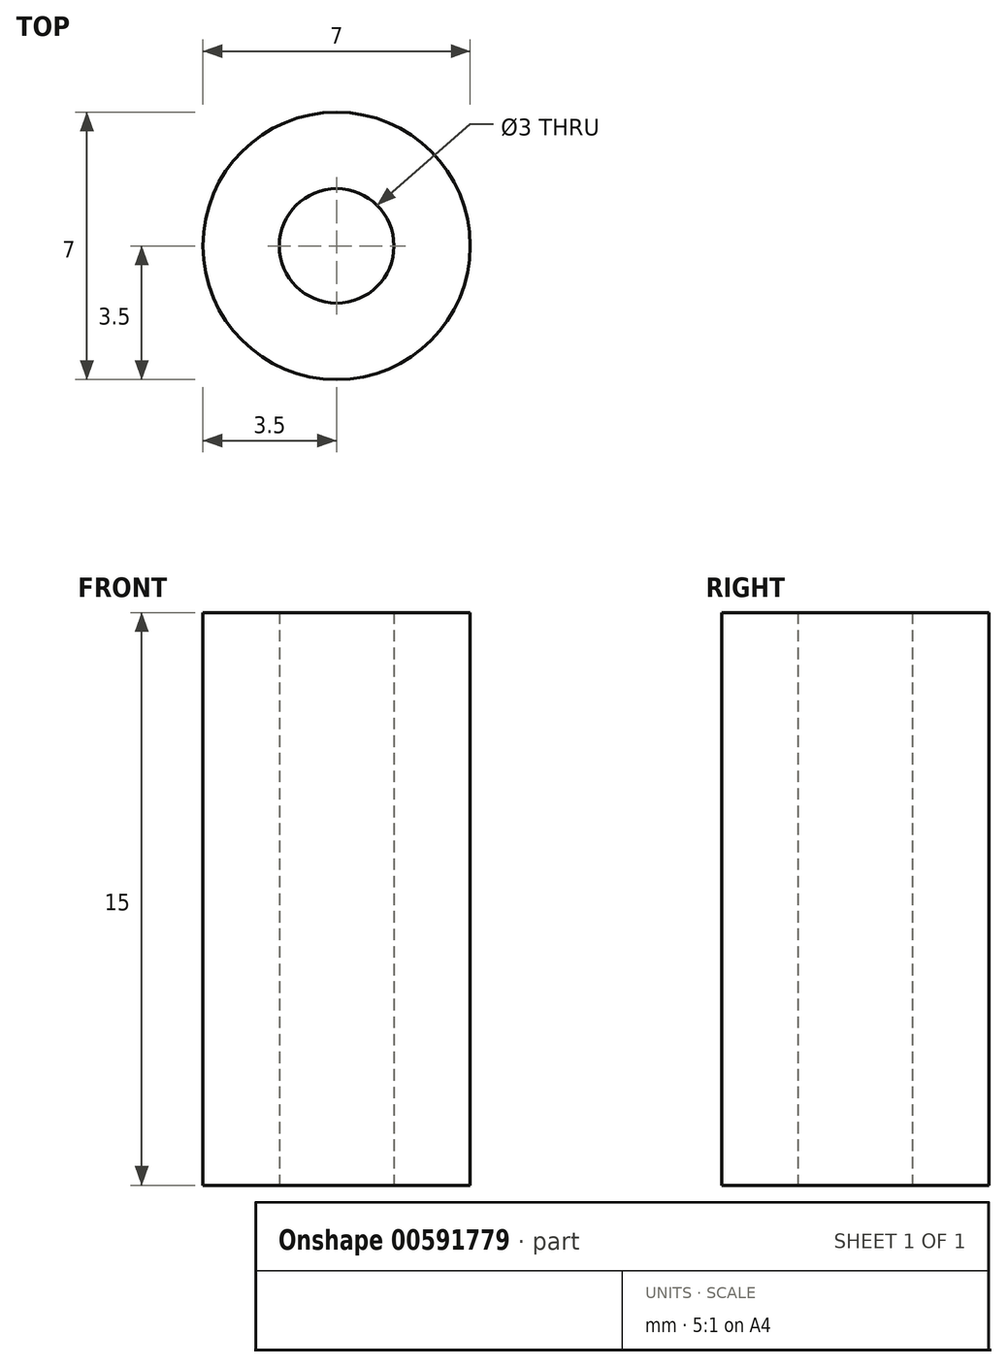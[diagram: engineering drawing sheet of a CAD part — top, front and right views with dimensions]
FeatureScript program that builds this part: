
annotation { "Feature Type Name" : "Feature", "Feature Type Description" : "" }
export const myFeature = defineFeature(function(context is Context, id is Id, definition is map)
    precondition{}
    {
        {
            var Q0;
            Q0=qCreatedBy(makeId("Top.planeOp"),FACE);
            var sketch = newSketch(context, id + "F0", { "sketchPlane" : qUnion([Q0])});
            skCircle(sketch, "E0", {"center": v(0, 0) * mm, "radius": 1.5 * mm});
            skCircle(sketch, "E1.0", {"center": v(0, 0) * mm, "radius": 3.5 * mm});
            skSolve(sketch);
        }
        {
            var Q0;
            Q0=makeQuery(id+"F0.imprint","IMPRINT",FACE,{"disambiguationData":[TD([[makeQuery(id+"F0.imprint","IMPRINT",EDGE,{"derivedFrom":sQuery(id+"F0.wireOp",EDGE,"E0")}),-1.0]])]});
            extrude(context, id + "F1", {"entities" : qUnion([Q0]), "endBound" : BoundingType.SYMMETRIC, "depth" : 15 * mm, "offsetDistance" : 25 * mm});
        }
    });
